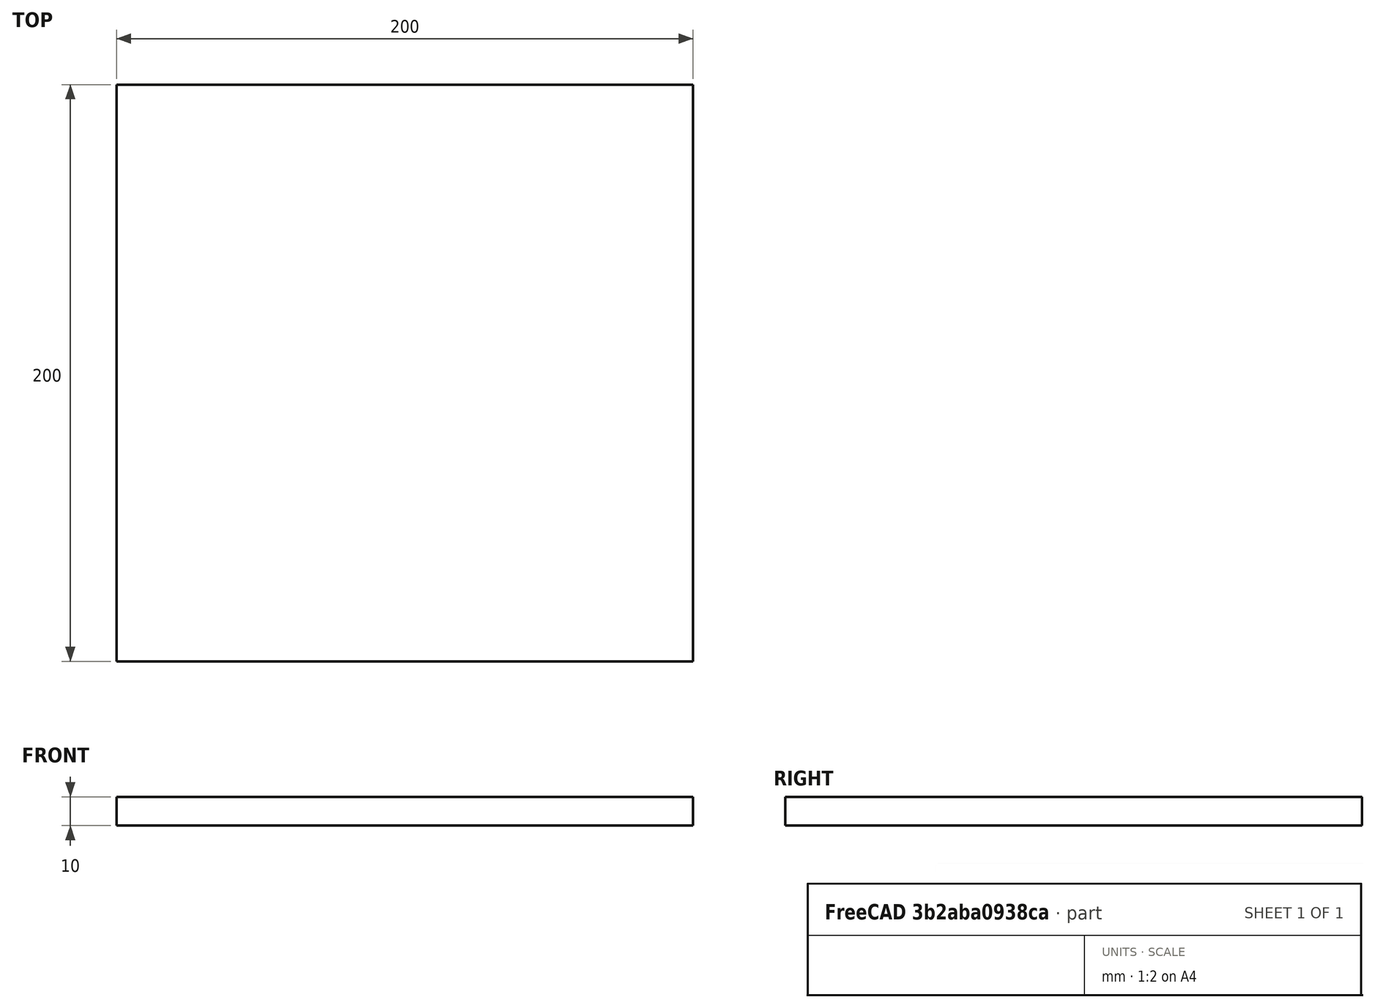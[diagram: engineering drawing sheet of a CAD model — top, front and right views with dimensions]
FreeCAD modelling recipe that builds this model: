
FCSTD DOCUMENT  (FreeCAD 0.19R24276 (Git))
Label: Osnovanie_katushki_1
License: All rights reserved
LicenseURL: http://en.wikipedia.org/wiki/All_rights_reserved
objects: Sketcher::SketchObject×1, PartDesign::Pad×1, PartDesign::Body×1
note: 4 computed .brp shape members not serialized (recipe doc carries the construction recipe); baked Part::Feature solids carry a one-line shape summary decoded from their .brp

FEATURE [Sketcher::SketchObject] Sketch
  FullyConstrained = true
  MapMode = 5
  Support = -> [XY_Plane]
  sketch-geometry (4):
    g0: LineSegment StartX=0 StartY=0 StartZ=0 EndX=200 EndY=0 EndZ=0
    g1: LineSegment StartX=200 StartY=0 StartZ=0 EndX=200 EndY=200 EndZ=0
    g2: LineSegment StartX=200 StartY=200 StartZ=0 EndX=0 EndY=200 EndZ=0
    g3: LineSegment StartX=0 StartY=200 StartZ=0 EndX=0 EndY=0 EndZ=0
  constraints (11):
    c: Coincident(g0,g1)
    c: Coincident(g1,g2)
    c: Coincident(g2,g3)
    c: Coincident(g3,g0)
    c: Horizontal(g0)
    c: Horizontal(g2)
    c: Vertical(g1)
    c: Vertical(g3)
    c: Coincident(g0,g-1)
    c: Distance(g1) = 200
    c: Distance(g0) = 200
FEATURE [PartDesign::Pad] Pad
  Direction = (1,1,1)
  Length = 10
  Length2 = 100
  Profile = -> Sketch
  Type = 0
FEATURE [PartDesign::Body] Body
  Group = -> [Sketch,Pad]
  Origin = -> Origin
  Tip = -> Pad
